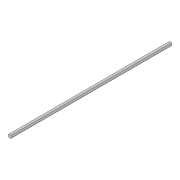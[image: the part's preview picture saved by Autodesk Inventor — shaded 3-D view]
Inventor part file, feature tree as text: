
AUTODESK INVENTOR PART (.ipt)
format: ipt  version: 2018 (Build 220112000, 112)  size: 75,264 bytes
history: native  units: in
note: dims shown in document units (in); Inventor stores cm internally (conversion verified against a paired STEP export)
features: extrude x1, sketch x1
ambient origin geometry x8: Origin, YZ Plane, XZ Plane, XY Plane, X Axis, Y Axis, Z Axis, Center Point
bodies: Solid1 (feature_tree)
feature tree (2):
  extrude  "Extrusion1"  Depth=9.5in TaperAngle=0.0deg
  sketch  "Sketch1"  dims[d0=0.1969in d1=9.5in d2=0.0in]
